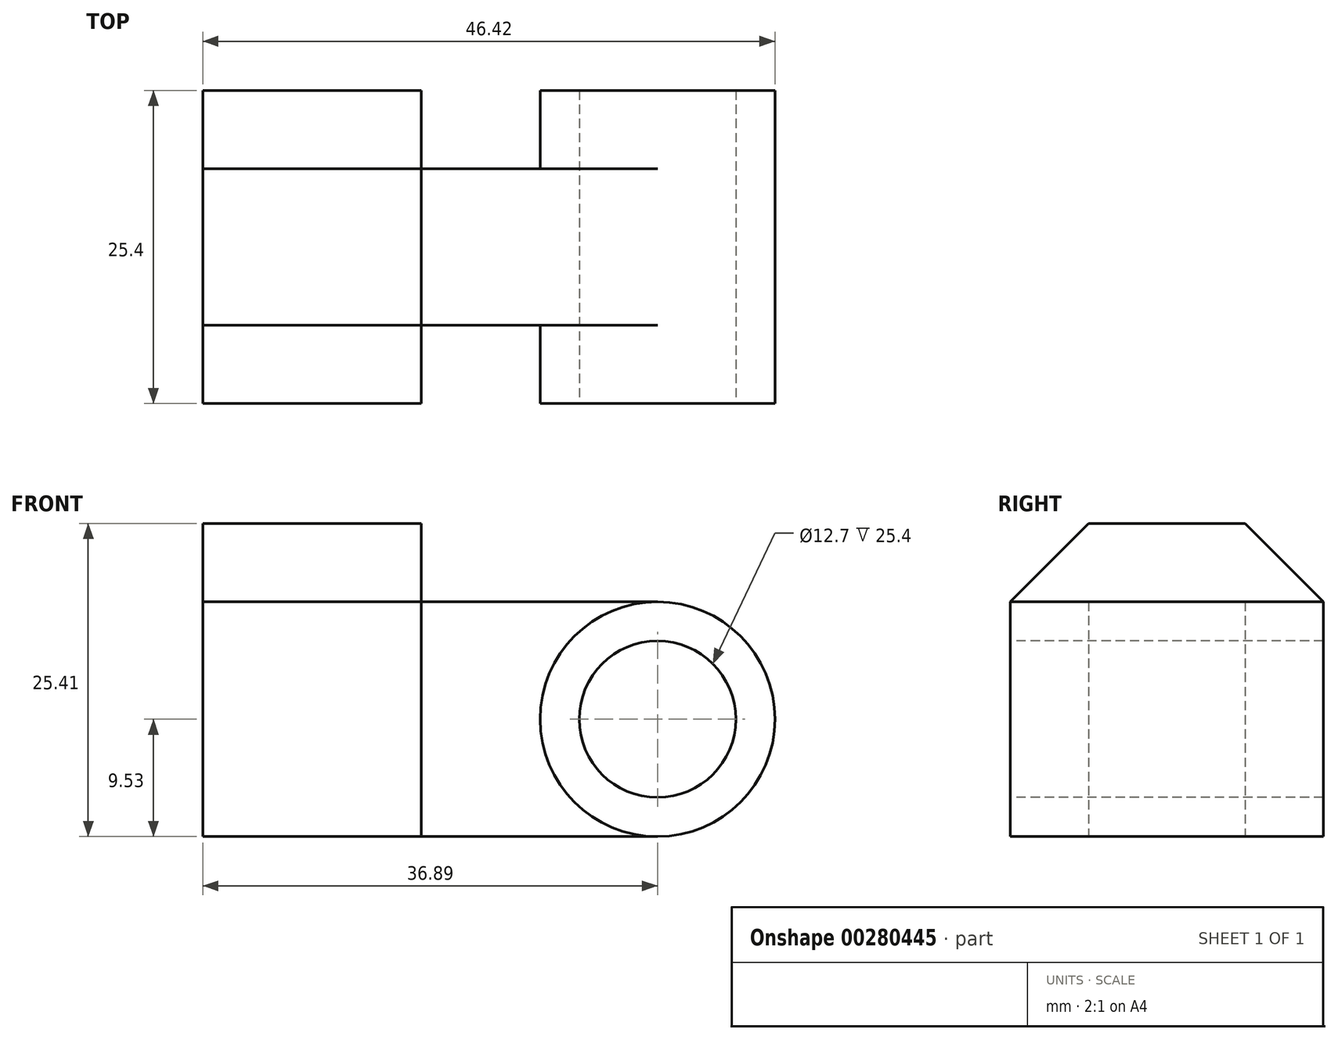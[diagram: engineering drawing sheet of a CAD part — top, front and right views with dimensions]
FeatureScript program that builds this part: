
annotation { "Feature Type Name" : "Feature", "Feature Type Description" : "" }
export const myFeature = defineFeature(function(context is Context, id is Id, definition is map)
    precondition{}
    {
        {
            var Q0;
            Q0=qCreatedBy(makeId("Front.planeOp"),FACE);
            var sketch = newSketch(context, id + "F0", { "sketchPlane" : qUnion([Q0])});
            skCircle(sketch, "E0", {"center": v(0, 0) * mm, "radius": 9.53 * mm});
            skSolve(sketch);
        }
        {
            var Q0;
            Q0 = qSketchRegion(id + "F0", true);
            extrude(context, id + "F1", {"entities" : qUnion([Q0]), "endBound" : BoundingType.SYMMETRIC, "oppositeDirection" : true, "depth" : 25.4 * mm});
        }
        {
            var Q0;
            Q0=qCreatedBy(makeId("Front.planeOp"),FACE);
            var sketch = newSketch(context, id + "F2", { "sketchPlane" : qUnion([Q0])});
            skCircle(sketch, "E1", {"center": v(0, 0) * mm, "radius": 6.35 * mm});
            skSolve(sketch);
        }
        {
            var Q0;
            Q0 = qSketchRegion(id + "F2", true);
            extrude(context, id + "F3", {"entities" : qUnion([Q0]), "operationType" : NewBodyOperationType.REMOVE, "endBound" : BoundingType.SYMMETRIC, "oppositeDirection" : true, "depth" : 25.4 * mm});
        }
        {
            var Q0;
            Q0=qCreatedBy(makeId("Front.planeOp"),FACE);
            var sketch = newSketch(context, id + "F4", { "sketchPlane" : qUnion([Q0])});
            skLineSegment(sketch, "E2", {"start": v(0, 9.53) * mm, "end": v(-19.18, 9.52) * mm});
            skLineSegment(sketch, "E3", {"start": v(-19.18, 9.52) * mm, "end": v(-19.18, -9.53) * mm});
            skLineSegment(sketch, "E4", {"start": v(-19.18, -9.53) * mm, "end": v(0, -9.53) * mm});
            skArc(sketch, "E5", {"start": v(0, 9.53) * mm, "mid": v(-9.53, 0) * mm, "end": v(0, -9.53) * mm});
            skSolve(sketch);
        }
        {
            var Q0;
            Q0 = qSketchRegion(id + "F4", true);
            extrude(context, id + "F5", {"entities" : qUnion([Q0]), "operationType" : NewBodyOperationType.ADD, "endBound" : BoundingType.SYMMETRIC, "depth" : 12.7 * mm});
        }
        {
            var Q0;
            Q0=qCreatedBy(makeId("Front.planeOp"),FACE);
            var sketch = newSketch(context, id + "F6", { "sketchPlane" : qUnion([Q0])});
            skLineSegment(sketch, "E6.bottom", {"start": v(-19.18, 15.88) * mm, "end": v(-36.89, 15.88) * mm});
            skLineSegment(sketch, "E6.top", {"start": v(-19.18, -9.52) * mm, "end": v(-36.89, -9.53) * mm});
            skLineSegment(sketch, "E6.left", {"start": v(-19.18, 15.88) * mm, "end": v(-19.18, -9.52) * mm});
            skLineSegment(sketch, "E6.right", {"start": v(-36.89, 15.88) * mm, "end": v(-36.89, -9.53) * mm});
            skSolve(sketch);
        }
        {
            var Q0;
            Q0 = qSketchRegion(id + "F6", true);
            extrude(context, id + "F7", {"entities" : qUnion([Q0]), "operationType" : NewBodyOperationType.ADD, "endBound" : BoundingType.SYMMETRIC, "oppositeDirection" : true, "depth" : 25.4 * mm});
        }
        {
            var Q0;
            Q0=qCreatedBy(makeId("Right.planeOp"),FACE);
            var sketch = newSketch(context, id + "F8", { "sketchPlane" : qUnion([Q0])});
            skLineSegment(sketch, "E7", {"start": v(12.7, 15.88) * mm, "end": v(12.7, 9.53) * mm});
            skLineSegment(sketch, "E8", {"start": v(12.7, 15.88) * mm, "end": v(6.35, 15.88) * mm});
            skLineSegment(sketch, "E9", {"start": v(6.35, 15.88) * mm, "end": v(12.7, 9.53) * mm});
            skLineSegment(sketch, "E10", {"start": v(-12.7, 15.88) * mm, "end": v(-12.7, 9.53) * mm});
            skLineSegment(sketch, "E11", {"start": v(-12.7, 15.88) * mm, "end": v(-6.35, 15.88) * mm});
            skLineSegment(sketch, "E12", {"start": v(-6.35, 15.88) * mm, "end": v(-12.7, 9.53) * mm});
            skSolve(sketch);
        }
        {
            var Q0;
            Q0 = qSketchRegion(id + "F8", true);
            extrude(context, id + "F9", {"entities" : qUnion([Q0]), "operationType" : NewBodyOperationType.REMOVE, "oppositeDirection" : true, "depth" : 38.1 * mm});
        }
    });
